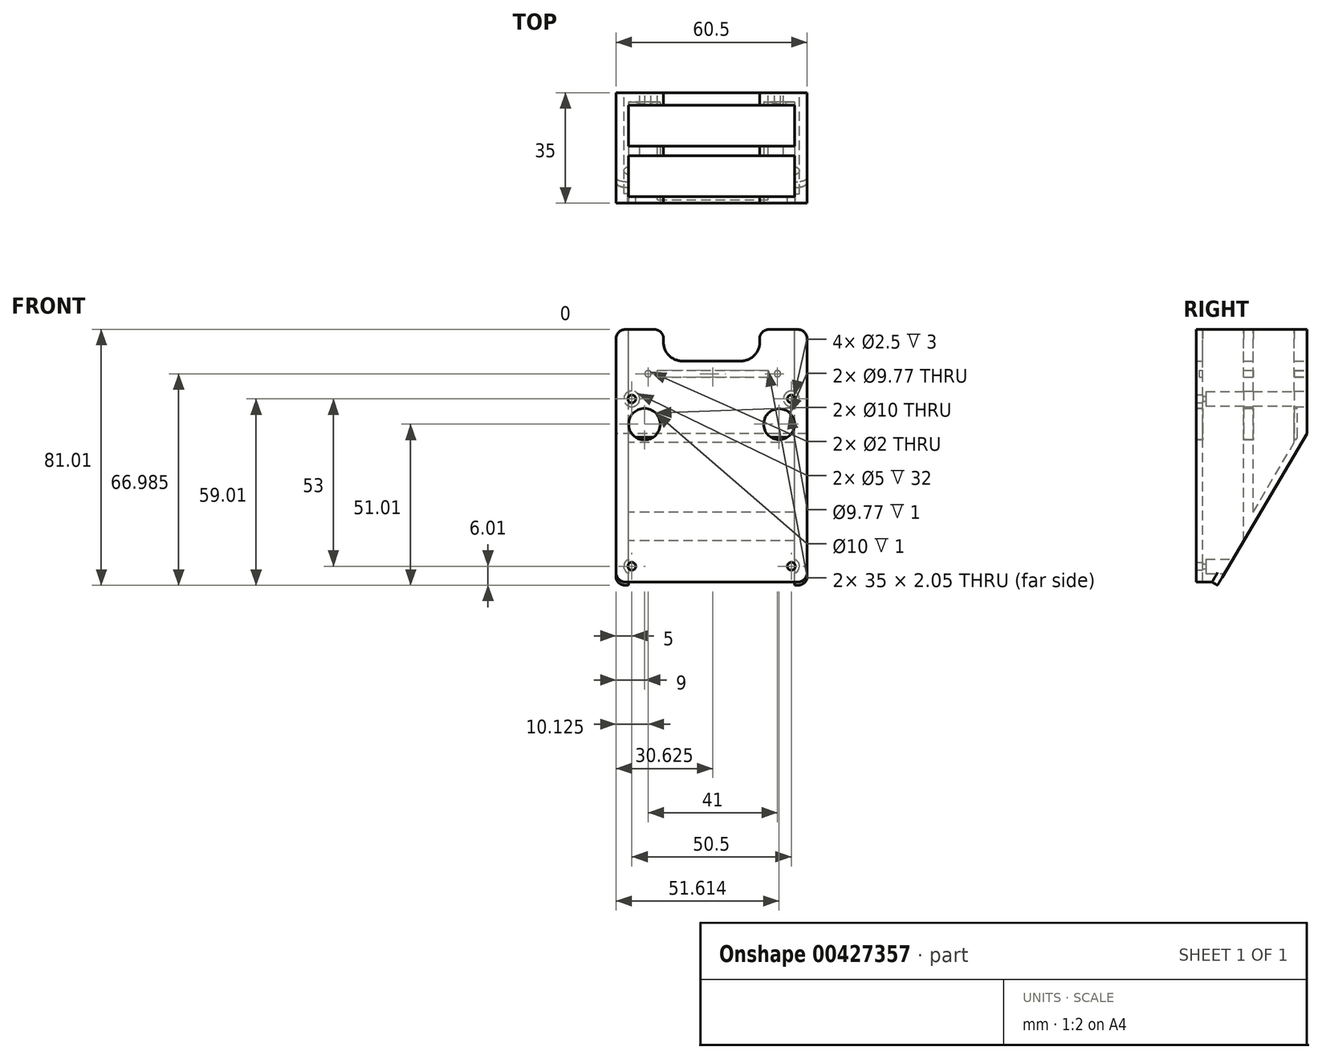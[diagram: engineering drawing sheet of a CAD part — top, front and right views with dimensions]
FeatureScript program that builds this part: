
annotation { "Feature Type Name" : "Feature", "Feature Type Description" : "" }
export const myFeature = defineFeature(function(context is Context, id is Id, definition is map)
    precondition{}
    {
        {
            var Q0;
            Q0=qCreatedBy(makeId("Front.planeOp"),FACE);
            var sketch = newSketch(context, id + "F0", { "sketchPlane" : qUnion([Q0])});
            skLineSegment(sketch, "E0.bottom", {"start": v(0, 0) * mm, "end": v(60.5, 0) * mm});
            skLineSegment(sketch, "E0.top", {"start": v(0, 80) * mm, "end": v(60.5, 80) * mm});
            skLineSegment(sketch, "E0.left", {"start": v(0, 0) * mm, "end": v(0, 80) * mm});
            skLineSegment(sketch, "E0.right", {"start": v(60.5, 0) * mm, "end": v(60.5, 80) * mm});
            skLineSegment(sketch, "E1", {"start": v(0, 63) * mm, "end": v(60.5, 63) * mm});
            skCircle(sketch, "E2", {"center": v(21, 76) * mm, "radius": 6 * mm});
            skCircle(sketch, "E3", {"center": v(39.5, 76) * mm, "radius": 6 * mm});
            skLineSegment(sketch, "E4", {"start": v(21, 70) * mm, "end": v(39.5, 70) * mm});
            skCircle(sketch, "E5", {"center": v(5, 58) * mm, "radius": 1.5 * mm});
            skCircle(sketch, "E6", {"center": v(5, 5) * mm, "radius": 1.5 * mm});
            skCircle(sketch, "E7", {"center": v(55.5, 58) * mm, "radius": 1.5 * mm});
            skCircle(sketch, "E8", {"center": v(55.5, 5) * mm, "radius": 1.5 * mm});
            skSolve(sketch);
        }
        {
            var Q0;
            {var subQ3=sQuery(id+"F0.wireOp",EDGE,"E1");Q0=makeQuery(id+"F0.imprint","IMPRINT",FACE,{"disambiguationData":[TD([[makeQuery(id+"F0.imprint","IMPRINT",EDGE,{"derivedFrom":subQ3}),1.0]])]});}
            var Q1;
            Q1=makeQuery(id+"F0.imprint","IMPRINT",FACE,{"disambiguationData":[TD([[makeQuery(id+"F0.imprint","IMPRINT",EDGE,{"derivedFrom":sQuery(id+"F0.wireOp",EDGE,"E5")}),1.0]])]});
            var Q2;
            Q2=makeQuery(id+"F0.imprint","IMPRINT",FACE,{"disambiguationData":[TD([[makeQuery(id+"F0.imprint","IMPRINT",EDGE,{"derivedFrom":sQuery(id+"F0.wireOp",EDGE,"E6")}),1.0]])]});
            var Q3;
            Q3=makeQuery(id+"F0.imprint","IMPRINT",FACE,{"disambiguationData":[TD([[makeQuery(id+"F0.imprint","IMPRINT",EDGE,{"derivedFrom":sQuery(id+"F0.wireOp",EDGE,"E8")}),1.0]])]});
            var Q4;
            Q4=makeQuery(id+"F0.imprint","IMPRINT",FACE,{"disambiguationData":[TD([[makeQuery(id+"F0.imprint","IMPRINT",EDGE,{"derivedFrom":sQuery(id+"F0.wireOp",EDGE,"E7")}),1.0]])]});
            var Q5;
            {var subQ1=sQuery(id+"F0.wireOp",EDGE,"E0.bottom");Q5=makeQuery(id+"F0.imprint","IMPRINT",FACE,{"disambiguationData":[TD([[makeQuery(id+"F0.imprint","IMPRINT",EDGE,{"derivedFrom":subQ1}),1.0]])]});}
            extrude(context, id + "F1", {"entities" : qUnion([Q0, Q1, Q2, Q3, Q4, Q5]), "depth" : 35 * mm});
        }
        {
            var Q0;
            {var subQ0=sQuery(id+"F0.wireOp",EDGE,"E0.top");Q0=makeQuery(id+"F1.opExtrude","SWEPT_FACE",FACE,{"disambiguationData":[OSD([subQ0]),TDD([makeQuery(id+"F0.imprint","IMPRINT",EDGE,{"disambiguationData":[TD([[makeQuery(id+"F0.imprint","INTERSECT",VERTEX,{"derivedFrom":[subQ0,sQuery(id+"F0.wireOp",EDGE,"E0.left")]}),-1.0]])],"derivedFrom":subQ0})])]});}
            var sketch = newSketch(context, id + "F2", { "sketchPlane" : qUnion([Q0])});
            skLineSegment(sketch, "E9", {"start": v(0, -4) * mm, "end": v(60.5, -4) * mm});
            skLineSegment(sketch, "E10", {"start": v(0, -17) * mm, "end": v(60.5, -17) * mm});
            skLineSegment(sketch, "E11", {"start": v(4, -4) * mm, "end": v(4, -17) * mm});
            skLineSegment(sketch, "E12", {"start": v(56.5, -4) * mm, "end": v(56.5, -17) * mm});
            skSolve(sketch);
        }
        {
            var Q0;
            {var subQ0=sQuery(id+"F2.wireOp",EDGE,"E11");Q0=makeQuery(id+"F2.imprint","IMPRINT",FACE,{"disambiguationData":[TD([[makeQuery(id+"F2.imprint","IMPRINT",EDGE,{"derivedFrom":subQ0}),1.0]])]});}
            var Q1;
            {var subQ0=sQuery(id+"F2.wireOp",EDGE,"E12");Q1=makeQuery(id+"F2.imprint","IMPRINT",FACE,{"disambiguationData":[TD([[makeQuery(id+"F2.imprint","IMPRINT",EDGE,{"derivedFrom":subQ0}),-1.0]])]});}
            extrude(context, id + "F3", {"entities" : qUnion([Q0, Q1]), "operationType" : NewBodyOperationType.REMOVE, "oppositeDirection" : true, "depth" : 80 * mm});
        }
        {
            var Q0;
            Q0=makeQuery(id+"F1.opExtrude","SWEPT_EDGE",EDGE,{"disambiguationData":[OSD([sQuery(id+"F0.wireOp",EDGE,"E0.top"),sQuery(id+"F0.wireOp",EDGE,"E0.right")])]});
            var Q1;
            Q1=makeQuery(id+"F1.opExtrude","SWEPT_EDGE",EDGE,{"disambiguationData":[OSD([sQuery(id+"F0.wireOp",EDGE,"E0.top"),sQuery(id+"F0.wireOp",EDGE,"E0.left")])]});
            var Q2;
            Q2=makeQuery(id+"F1.opExtrude","SWEPT_EDGE",EDGE,{"disambiguationData":[OSD([sQuery(id+"F0.wireOp",EDGE,"E0.bottom"),sQuery(id+"F0.wireOp",EDGE,"E0.left")])]});
            var Q3;
            Q3=makeQuery(id+"F1.opExtrude","SWEPT_EDGE",EDGE,{"disambiguationData":[OSD([sQuery(id+"F0.wireOp",EDGE,"E0.bottom"),sQuery(id+"F0.wireOp",EDGE,"E0.right")])]});
            var Q4;
            {var subQ0=sQuery(id+"F0.wireOp",EDGE,"E2");var subQ2=sQuery(id+"F0.wireOp",EDGE,"E0.top");Q4=makeQuery(id+"F3.boolean.opBoolean","SPLIT",EDGE,{"disambiguationData":[TD([makeQuery(id+"F3.opExtrude","SWEPT_FACE",FACE,{"disambiguationData":[OSD([sQuery(id+"F2.wireOp",EDGE,"E10")])]})])],"derivedFrom":makeQuery(id+"F1.opExtrude","SWEPT_EDGE",EDGE,{"disambiguationData":[OSD([subQ2,subQ0])]})});}
            var Q5;
            {var subQ0=sQuery(id+"F0.wireOp",EDGE,"E3");var subQ2=sQuery(id+"F0.wireOp",EDGE,"E0.top");Q5=makeQuery(id+"F3.boolean.opBoolean","SPLIT",EDGE,{"disambiguationData":[TD([makeQuery(id+"F3.opExtrude","SWEPT_FACE",FACE,{"disambiguationData":[OSD([sQuery(id+"F2.wireOp",EDGE,"E10")])]})])],"derivedFrom":makeQuery(id+"F1.opExtrude","SWEPT_EDGE",EDGE,{"disambiguationData":[OSD([subQ2,subQ0])]})});}
            var Q6;
            {var subQ0=sQuery(id+"F0.wireOp",EDGE,"E3");var subQ2=sQuery(id+"F0.wireOp",EDGE,"E0.top");Q6=makeQuery(id+"F3.boolean.opBoolean","SPLIT",EDGE,{"disambiguationData":[TD([makeQuery(id+"F3.opExtrude","SWEPT_FACE",FACE,{"disambiguationData":[OSD([sQuery(id+"F2.wireOp",EDGE,"E9")])]})])],"derivedFrom":makeQuery(id+"F1.opExtrude","SWEPT_EDGE",EDGE,{"disambiguationData":[OSD([subQ2,subQ0])]})});}
            var Q7;
            {var subQ0=sQuery(id+"F0.wireOp",EDGE,"E2");var subQ2=sQuery(id+"F0.wireOp",EDGE,"E0.top");Q7=makeQuery(id+"F3.boolean.opBoolean","SPLIT",EDGE,{"disambiguationData":[TD([makeQuery(id+"F3.opExtrude","SWEPT_FACE",FACE,{"disambiguationData":[OSD([sQuery(id+"F2.wireOp",EDGE,"E9")])]})])],"derivedFrom":makeQuery(id+"F1.opExtrude","SWEPT_EDGE",EDGE,{"disambiguationData":[OSD([subQ2,subQ0])]})});}
            fillet(context, id + "F4", {"entities" : qUnion([Q0, Q1, Q2, Q3, Q4, Q5, Q6, Q7]), "radius" : 3 * mm, "tangentPropagation" : true, "allowEdgeOverflow" : false});
        }
        {
            var Q0;
            Q0=makeQuery(id+"F1.opExtrude","CAP_FACE",FACE,{"disambiguationData":[OSD([sQuery(id+"F0.wireOp",EDGE,"E0.bottom"),sQuery(id+"F0.wireOp",EDGE,"E0.top"),sQuery(id+"F0.wireOp",EDGE,"E0.left"),sQuery(id+"F0.wireOp",EDGE,"E0.right"),sQuery(id+"F0.wireOp",EDGE,"E2"),sQuery(id+"F0.wireOp",EDGE,"E3"),sQuery(id+"F0.wireOp",EDGE,"E4")])],"isStart":false});
            var sketch = newSketch(context, id + "F5", { "sketchPlane" : qUnion([Q0])});
            skCircle(sketch, "E13", {"center": v(9, 50) * mm, "radius": 5 * mm});
            skCircle(sketch, "E14", {"center": v(51.61, 50) * mm, "radius": 4.89 * mm});
            skSolve(sketch);
        }
        {
            var Q0;
            Q0 = qSketchRegion(id + "F5", true);
            extrude(context, id + "F6", {"entities" : qUnion([Q0]), "operationType" : NewBodyOperationType.REMOVE, "oppositeDirection" : true, "depth" : 32 * mm});
        }
        {
            var Q0;
            {var subQ1=sQuery(id+"F0.wireOp",EDGE,"E0.bottom");Q0=makeQuery(id+"F0.imprint","IMPRINT",FACE,{"disambiguationData":[TD([[makeQuery(id+"F0.imprint","IMPRINT",EDGE,{"derivedFrom":subQ1}),1.0]])]});}
            var sketch = newSketch(context, id + "F7", { "sketchPlane" : qUnion([Q0])});
            skLineSegment(sketch, "E15.bottom", {"start": v(13.12, 64.95) * mm, "end": v(48.12, 64.95) * mm});
            skLineSegment(sketch, "E15.top", {"start": v(13.12, 67) * mm, "end": v(48.12, 67) * mm});
            skLineSegment(sketch, "E15.left", {"start": v(13.12, 64.95) * mm, "end": v(13.12, 67) * mm});
            skLineSegment(sketch, "E15.right", {"start": v(48.12, 64.95) * mm, "end": v(48.12, 67) * mm});
            skLineSegment(sketch, "E16", {"start": v(10.12, 65.98) * mm, "end": v(13.12, 65.98) * mm});
            skLineSegment(sketch, "E17", {"start": v(51.13, 65.98) * mm, "end": v(48.12, 65.98) * mm});
            skSolve(sketch);
        }
        {
            var Q0;
            Q0 = qSketchRegion(id + "F7", true);
            extrude(context, id + "F8", {"entities" : qUnion([Q0]), "operationType" : NewBodyOperationType.REMOVE, "depth" : 34 * mm});
        }
        {
            var Q0;
            Q0=sQuery(id+"F7.wireOp",VERTEX,"E17.start");
            var Q1;
            Q1=sQuery(id+"F7.wireOp",VERTEX,"E16.start");
            var Q2;
            Q2=makeQuery(id+"F1.opExtrude","SWEPT_BODY",BODY,{"disambiguationData":[OSD([sQuery(id+"F0.wireOp",EDGE,"E0.bottom"),sQuery(id+"F0.wireOp",EDGE,"E0.top"),sQuery(id+"F0.wireOp",EDGE,"E0.left"),sQuery(id+"F0.wireOp",EDGE,"E0.right"),sQuery(id+"F0.wireOp",EDGE,"E2"),sQuery(id+"F0.wireOp",EDGE,"E3"),sQuery(id+"F0.wireOp",EDGE,"E4")])]});
            hole(context, id + "F9", {"style" : HoleStyle.C_BORE, "endStyle" : HoleEndStyle.BLIND, "oppositeDirection" : true, "holeDiameter" : 2 * mm, "cBoreDiameter" : 5 * mm, "cBoreDepth" : 0 * mm, "holeDepth" : 5 * mm, "isTappedThrough" : true, "tappedDepth" : 12 * mm, "tapClearance" : 3, "startFromSketch" : true, "locations" : qUnion([Q0, Q1]), "scope" : qUnion([Q2])});
        }
        {
            var Q0;
            Q0=makeQuery(id+"F1.opExtrude","SWEPT_FACE",FACE,{"disambiguationData":[OSD([sQuery(id+"F0.wireOp",EDGE,"E0.right")])]});
            var sketch = newSketch(context, id + "F10", { "sketchPlane" : qUnion([Q0])});
            skLineSegment(sketch, "E18", {"start": v(0, -0.44) * mm, "end": v(0, 51) * mm});
            skLineSegment(sketch, "E19", {"start": v(0, 51) * mm, "end": v(-35, 51) * mm});
            skLineSegment(sketch, "E20", {"start": v(-30, 51) * mm, "end": v(-30, 0) * mm});
            skLineSegment(sketch, "E21", {"start": v(-35, 3) * mm, "end": v(-35, 51) * mm});
            skLineSegment(sketch, "E22", {"start": v(0, 51) * mm, "end": v(-30, 0) * mm});
            skLineSegment(sketch, "E23", {"start": v(0, 0) * mm, "end": v(-30, 0) * mm});
            skSolve(sketch);
        }
        {
            var Q0;
            {var subQ0=sQuery(id+"F10.wireOp",EDGE,"E18");var subQ1=sQuery(id+"F0.wireOp",EDGE,"E0.right");var subQ2=makeQuery(id+"F4.opFillet","BLEND_EDGE",EDGE,{"blendedFrom":[makeQuery(id+"F1.opExtrude","SWEPT_EDGE",EDGE,{"disambiguationData":[OSD([sQuery(id+"F0.wireOp",EDGE,"E0.bottom"),subQ1])]}),makeQuery(id+"F1.opExtrude","SWEPT_FACE",FACE,{"disambiguationData":[OSD([subQ1])]})],"blendedInto":[makeQuery(id+"F1.opExtrude","SWEPT_FACE",FACE,{"disambiguationData":[OSD([subQ1])]})]});var subQ3=makeQuery(id+"F10.imprint","INTERSECT",VERTEX,{"derivedFrom":[subQ2,subQ0]});Q0=makeQuery(id+"F10.imprint","IMPRINT",FACE,{"disambiguationData":[TD([[makeQuery(id+"F10.imprint","IMPRINT",EDGE,{"disambiguationData":[TD([[subQ3,-1.0]])],"derivedFrom":subQ0}),1.0]])]});}
            var Q1;
            {var subQ4=sQuery(id+"F10.wireOp",EDGE,"E23");Q1=makeQuery(id+"F10.imprint","IMPRINT",FACE,{"disambiguationData":[TD([[makeQuery(id+"F10.imprint","IMPRINT",EDGE,{"derivedFrom":subQ4}),-1.0]])]});}
            extrude(context, id + "F11", {"entities" : qUnion([Q0, Q1]), "operationType" : NewBodyOperationType.REMOVE, "oppositeDirection" : true, "depth" : 70 * mm});
        }
        {
            var Q0;
            Q0=makeQuery(id+"F11.boolean.opBoolean","COPY",FACE,{"derivedFrom":makeQuery(id+"F11.opExtrude","SWEPT_FACE",FACE,{"disambiguationData":[OSD([sQuery(id+"F10.wireOp",EDGE,"E22")])]})});
            var sketch = newSketch(context, id + "F12", { "sketchPlane" : qUnion([Q0])});
            skLineSegment(sketch, "E24", {"start": v(-60.5, 43.96) * mm, "end": v(0, 43.96) * mm});
            skLineSegment(sketch, "E25", {"start": v(0, 43.96) * mm, "end": v(0, -11.73) * mm});
            skLineSegment(sketch, "E26", {"start": v(0, -11.73) * mm, "end": v(0, -12.21) * mm});
            skLineSegment(sketch, "E27", {"start": v(-3, -15.21) * mm, "end": v(-57.5, -15.21) * mm});
            skLineSegment(sketch, "E28", {"start": v(-60.5, -12.21) * mm, "end": v(-60.5, 43.96) * mm});
            skPoint(sketch, "E29.visualSharp", {"position": v(-60.5, -15.21) * mm});
            skArc(sketch, "E29.filletArc", {"start": v(-60.5, -12.21) * mm, "mid": v(-59.62, -14.33) * mm, "end": v(-57.5, -15.21) * mm});
            skPoint(sketch, "E30.visualSharp", {"position": v(0, -15.21) * mm});
            skArc(sketch, "E30.filletArc", {"start": v(-3, -15.21) * mm, "mid": v(-0.88, -14.33) * mm, "end": v(0, -12.21) * mm});
            skSolve(sketch);
        }
        {
            var Q0;
            Q0 = qSketchRegion(id + "F12", true);
            extrude(context, id + "F13", {"entities" : qUnion([Q0]), "operationType" : NewBodyOperationType.ADD, "depth" : 2 * mm});
        }
        {
            var Q0;
            {var subQ0=sQuery(id+"F0.wireOp",EDGE,"E0.top");Q0=makeQuery(id+"F1.opExtrude","SWEPT_FACE",FACE,{"disambiguationData":[OSD([subQ0]),TDD([makeQuery(id+"F0.imprint","IMPRINT",EDGE,{"disambiguationData":[TD([[makeQuery(id+"F0.imprint","INTERSECT",VERTEX,{"derivedFrom":[subQ0,sQuery(id+"F0.wireOp",EDGE,"E0.left")]}),-1.0]])],"derivedFrom":subQ0})])]});}
            var sketch = newSketch(context, id + "F14", { "sketchPlane" : qUnion([Q0])});
            skLineSegment(sketch, "E31.bottom", {"start": v(4, -20) * mm, "end": v(56.5, -20) * mm});
            skLineSegment(sketch, "E31.top", {"start": v(4, -33) * mm, "end": v(56.5, -33) * mm});
            skLineSegment(sketch, "E31.left", {"start": v(4, -20) * mm, "end": v(4, -33) * mm});
            skLineSegment(sketch, "E31.right", {"start": v(56.5, -20) * mm, "end": v(56.5, -33) * mm});
            skLineSegment(sketch, "E32.bottom", {"start": v(0, 0) * mm, "end": v(60.5, 0) * mm});
            skLineSegment(sketch, "E32.top", {"start": v(0, 3.88) * mm, "end": v(60.5, 3.88) * mm});
            skLineSegment(sketch, "E32.left", {"start": v(0, 0) * mm, "end": v(0, 3.88) * mm});
            skLineSegment(sketch, "E32.right", {"start": v(60.5, 0) * mm, "end": v(60.5, 3.88) * mm});
            skSolve(sketch);
        }
        {
            var Q0;
            Q0 = qSketchRegion(id + "F14", true);
            extrude(context, id + "F15", {"entities" : qUnion([Q0]), "operationType" : NewBodyOperationType.REMOVE, "oppositeDirection" : true, "depth" : 85 * mm});
        }
        {
            var Q0;
            Q0=sQuery(id+"F0.wireOp",VERTEX,"E5.center");
            var Q1;
            Q1=sQuery(id+"F0.wireOp",VERTEX,"E7.center");
            var Q2;
            Q2=sQuery(id+"F0.wireOp",VERTEX,"E8.center");
            var Q3;
            Q3=sQuery(id+"F0.wireOp",VERTEX,"E6.center");
            var Q4;
            Q4=makeQuery(id+"F1.opExtrude","SWEPT_BODY",BODY,{"disambiguationData":[OSD([sQuery(id+"F0.wireOp",EDGE,"E0.bottom"),sQuery(id+"F0.wireOp",EDGE,"E0.top"),sQuery(id+"F0.wireOp",EDGE,"E0.left"),sQuery(id+"F0.wireOp",EDGE,"E0.right"),sQuery(id+"F0.wireOp",EDGE,"E2"),sQuery(id+"F0.wireOp",EDGE,"E3"),sQuery(id+"F0.wireOp",EDGE,"E4")])]});
            hole(context, id + "F16", {"style" : HoleStyle.C_BORE, "endStyle" : HoleEndStyle.THROUGH, "oppositeDirection" : true, "holeDiameter" : 2.5 * mm, "cBoreDiameter" : 5 * mm, "cBoreDepth" : 32 * mm, "isTappedThrough" : true, "tappedDepth" : 12 * mm, "tapClearance" : 3, "startFromSketch" : true, "locations" : qUnion([Q0, Q1, Q2, Q3]), "scope" : qUnion([Q4])});
        }
    });
